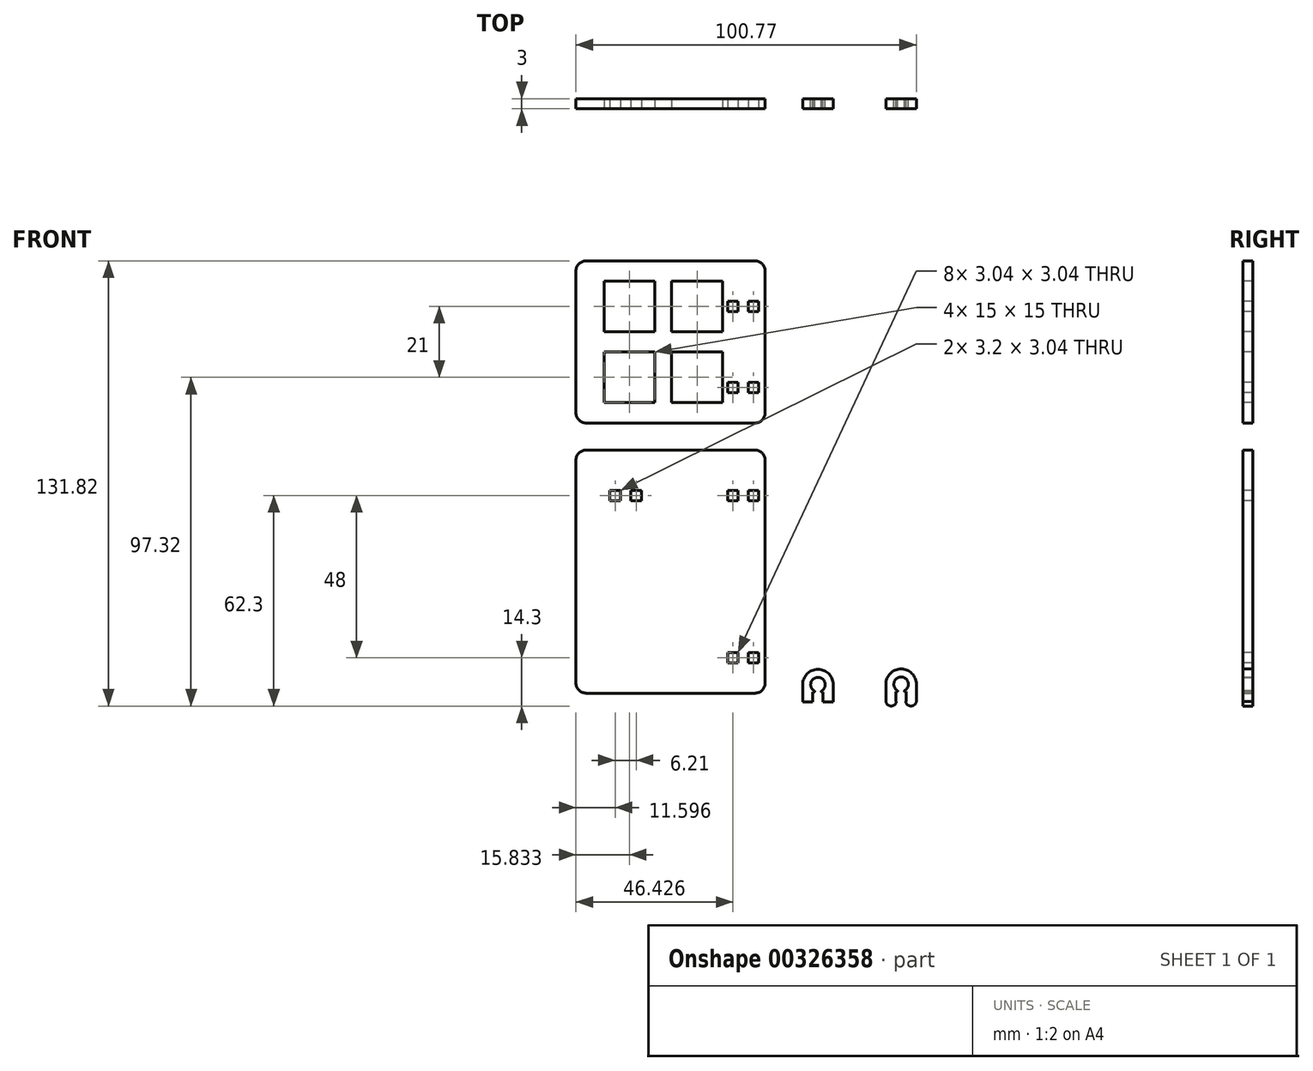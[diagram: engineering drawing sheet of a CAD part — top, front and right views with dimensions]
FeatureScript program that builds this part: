
annotation { "Feature Type Name" : "Feature", "Feature Type Description" : "" }
export const myFeature = defineFeature(function(context is Context, id is Id, definition is map)
    precondition{}
    {
        {
            var Q0;
            Q0=qCreatedBy(makeId("Front.planeOp"),FACE);
            var sketch = newSketch(context, id + "F0", { "sketchPlane" : qUnion([Q0])});
            skArc(sketch, "E0", {"start": v(1.01, 0.63) * mm, "mid": v(0.03, 4.67) * mm, "end": v(-1.07, 0.66) * mm});
            skPoint(sketch, "E0.centerSnap0", {"position": v(-1.52, 2.52) * mm});
            skArc(sketch, "E1", {"start": v(4.53, 2.52) * mm, "mid": v(0, 7.05) * mm, "end": v(-4.53, 2.52) * mm});
            skLineSegment(sketch, "E2", {"start": v(-4.53, 2.52) * mm, "end": v(-4.53, -2.63) * mm});
            skLineSegment(sketch, "E3", {"start": v(4.52, 2.52) * mm, "end": v(4.53, -2.63) * mm});
            skPoint(sketch, "E3.startSnap0", {"position": v(1.52, 2.52) * mm});
            skPoint(sketch, "E4.orphan", {"position": v(-1.52, 4.05) * mm});
            skPoint(sketch, "E5.orphan", {"position": v(1.52, 4.05) * mm});
            skLineSegment(sketch, "E6", {"start": v(-1.08, 0.37) * mm, "end": v(-1.52, 0.37) * mm});
            skLineSegment(sketch, "E7", {"start": v(1.07, 0.37) * mm, "end": v(1.53, 0.37) * mm});
            skArc(sketch, "E8", {"start": v(-1.08, 0.37) * mm, "mid": v(-1, 0.52) * mm, "end": v(-1.08, 0.67) * mm});
            skArc(sketch, "E9", {"start": v(1.01, 0.63) * mm, "mid": v(0.96, 0.47) * mm, "end": v(1.1, 0.37) * mm});
            skPoint(sketch, "E10.orphan", {"position": v(0, 0.37) * mm});
            skPoint(sketch, "E11.start.orphan", {"position": v(-2.15, 2.53) * mm});
            skPoint(sketch, "E12.start.orphan", {"position": v(2.15, 2.53) * mm});
            skLineSegment(sketch, "E13", {"start": v(-1.52, -2.63) * mm, "end": v(-1.52, 0.37) * mm});
            skLineSegment(sketch, "E14", {"start": v(1.53, -2.63) * mm, "end": v(1.53, 0.38) * mm});
            skPoint(sketch, "E15", {"position": v(-1.52, -2.63) * mm});
            skPoint(sketch, "E16", {"position": v(1.53, -2.63) * mm});
            skLineSegment(sketch, "E17", {"start": v(-1.52, -2.63) * mm, "end": v(-4.53, -2.63) * mm});
            skLineSegment(sketch, "E18", {"start": v(1.53, -2.63) * mm, "end": v(4.53, -2.63) * mm});
            skPoint(sketch, "E19.start.orphan", {"position": v(0, 4.05) * mm});
            skArc(sketch, "E20", {"start": v(25.63, 0.75) * mm, "mid": v(24.65, 4.8) * mm, "end": v(23.54, 0.78) * mm});
            skPoint(sketch, "E20.centerSnap0", {"position": v(23.09, 2.64) * mm});
            skArc(sketch, "E21", {"start": v(29.14, 2.64) * mm, "mid": v(24.61, 7.17) * mm, "end": v(20.09, 2.64) * mm});
            skLineSegment(sketch, "E22", {"start": v(20.09, 2.64) * mm, "end": v(20.09, -2.5) * mm});
            skLineSegment(sketch, "E23", {"start": v(29.14, 2.64) * mm, "end": v(29.14, -2.5) * mm});
            skPoint(sketch, "E23.startSnap0", {"position": v(26.14, 2.64) * mm});
            skPoint(sketch, "E24.orphan", {"position": v(23.1, 4.17) * mm});
            skPoint(sketch, "E25.orphan", {"position": v(26.13, 4.16) * mm});
            skLineSegment(sketch, "E26", {"start": v(23.53, 0.5) * mm, "end": v(23.09, 0.5) * mm});
            skLineSegment(sketch, "E27", {"start": v(25.68, 0.5) * mm, "end": v(26.14, 0.5) * mm});
            skArc(sketch, "E28", {"start": v(23.53, 0.5) * mm, "mid": v(23.62, 0.64) * mm, "end": v(23.53, 0.79) * mm});
            skArc(sketch, "E29", {"start": v(25.63, 0.75) * mm, "mid": v(25.57, 0.58) * mm, "end": v(25.72, 0.5) * mm});
            skPoint(sketch, "E30.orphan", {"position": v(24.61, 0.5) * mm});
            skPoint(sketch, "E31.start.orphan", {"position": v(22.46, 2.64) * mm});
            skPoint(sketch, "E32.start.orphan", {"position": v(26.76, 2.64) * mm});
            skLineSegment(sketch, "E33", {"start": v(23.09, -2.5) * mm, "end": v(23.09, 0.5) * mm});
            skLineSegment(sketch, "E34", {"start": v(26.14, -2.5) * mm, "end": v(26.14, 0.5) * mm});
            skPoint(sketch, "E35", {"position": v(23.09, -2.5) * mm});
            skPoint(sketch, "E36", {"position": v(26.14, -2.5) * mm});
            skPoint(sketch, "E37.start.orphan", {"position": v(24.61, 4.17) * mm});
            skLineSegment(sketch, "E38", {"start": v(23.09, -2.5) * mm, "end": v(23.29, -2.5) * mm});
            skLineSegment(sketch, "E39", {"start": v(26.14, -2.5) * mm, "end": v(25.94, -2.5) * mm});
            skArc(sketch, "E40", {"start": v(20.09, -2.5) * mm, "mid": v(21.69, -3.82) * mm, "end": v(23.29, -2.5) * mm});
            skArc(sketch, "E41", {"start": v(25.94, -2.5) * mm, "mid": v(27.54, -3.82) * mm, "end": v(29.14, -2.5) * mm});
            skPoint(sketch, "E42.end.orphan", {"position": v(23.09, -3.5) * mm});
            skPoint(sketch, "E43.orphan", {"position": v(26.14, -3.5) * mm});
            skSolve(sketch);
        }
        {
            var Q0;
            Q0=makeQuery(id+"F0.imprint","IMPRINT",FACE,{"disambiguationData":[TD([[makeQuery(id+"F0.imprint","IMPRINT",EDGE,{"derivedFrom":sQuery(id+"F0.wireOp",EDGE,"E0")}),-1.0]])]});
            var Q1;
            {var subQ1=sQuery(id+"F0.wireOp",EDGE,"E20");Q1=makeQuery(id+"F0.imprint","IMPRINT",FACE,{"disambiguationData":[TD([[makeQuery(id+"F0.imprint","IMPRINT",EDGE,{"derivedFrom":subQ1}),-1.0]])]});}
            extrude(context, id + "F1", {"entities" : qUnion([Q0, Q1]), "depth" : 3 * mm});
        }
        {
            var Q0;
            Q0=qCreatedBy(makeId("Front.planeOp"),FACE);
            var sketch = newSketch(context, id + "F2", { "sketchPlane" : qUnion([Q0])});
            skLineSegment(sketch, "E44.bottom", {"start": v(-71.63, 0) * mm, "end": v(-15.63, 0) * mm});
            skLineSegment(sketch, "E44.left", {"start": v(-71.63, 0) * mm, "end": v(-71.63, 72) * mm});
            skLineSegment(sketch, "E44.right", {"start": v(-15.63, 0) * mm, "end": v(-15.63, 72) * mm});
            skLineSegment(sketch, "E45", {"start": v(-71.63, 80) * mm, "end": v(-71.63, 128) * mm});
            skLineSegment(sketch, "E46", {"start": v(-15.63, 80) * mm, "end": v(-15.63, 128) * mm});
            skLineSegment(sketch, "E47", {"start": v(-15.63, 128) * mm, "end": v(-71.63, 128) * mm});
            skLineSegment(sketch, "E48", {"start": v(-71.63, 72) * mm, "end": v(-15.63, 72) * mm});
            skLineSegment(sketch, "E49", {"start": v(-71.63, 80) * mm, "end": v(-15.63, 80) * mm});
            skSolve(sketch);
        }
        {
            var Q0;
            Q0=makeQuery(id+"F2.imprint","IMPRINT",FACE,{"disambiguationData":[TD([[makeQuery(id+"F2.imprint","IMPRINT",EDGE,{"derivedFrom":sQuery(id+"F2.wireOp",EDGE,"E45")}),-1.0]])]});
            var Q1;
            Q1=makeQuery(id+"F2.imprint","IMPRINT",FACE,{"disambiguationData":[TD([[makeQuery(id+"F2.imprint","IMPRINT",EDGE,{"derivedFrom":sQuery(id+"F2.wireOp",EDGE,"E44.bottom")}),1.0]])]});
            extrude(context, id + "F3", {"entities" : qUnion([Q0, Q1]), "depth" : 3 * mm});
        }
        {
            var Q0;
            Q0=makeQuery(id+"F3.opExtrude","CAP_FACE",FACE,{"disambiguationData":[OSD([sQuery(id+"F2.wireOp",EDGE,"E45"),sQuery(id+"F2.wireOp",EDGE,"E46"),sQuery(id+"F2.wireOp",EDGE,"E47"),sQuery(id+"F2.wireOp",EDGE,"E49")])],"isStart":false});
            var sketch = newSketch(context, id + "F4", { "sketchPlane" : qUnion([Q0])});
            skLineSegment(sketch, "E50.bottom", {"start": v(-23.68, 12) * mm, "end": v(-26.72, 12) * mm});
            skLineSegment(sketch, "E50.top", {"start": v(-23.68, 8.96) * mm, "end": v(-26.72, 8.96) * mm});
            skLineSegment(sketch, "E50.left", {"start": v(-23.68, 12) * mm, "end": v(-23.68, 8.96) * mm});
            skLineSegment(sketch, "E50.right", {"start": v(-26.72, 12) * mm, "end": v(-26.72, 8.96) * mm});
            skLineSegment(sketch, "E51.bottom", {"start": v(-20.67, 12) * mm, "end": v(-17.63, 12) * mm});
            skLineSegment(sketch, "E51.top", {"start": v(-20.67, 8.96) * mm, "end": v(-17.63, 8.96) * mm});
            skLineSegment(sketch, "E51.left", {"start": v(-20.67, 12) * mm, "end": v(-20.67, 8.96) * mm});
            skLineSegment(sketch, "E51.right", {"start": v(-17.63, 12) * mm, "end": v(-17.63, 8.96) * mm});
            skLineSegment(sketch, "E52.bottom", {"start": v(-23.68, 60) * mm, "end": v(-26.72, 60) * mm});
            skLineSegment(sketch, "E52.top", {"start": v(-23.68, 56.96) * mm, "end": v(-26.72, 56.96) * mm});
            skLineSegment(sketch, "E52.left", {"start": v(-23.68, 60) * mm, "end": v(-23.68, 56.96) * mm});
            skLineSegment(sketch, "E52.right", {"start": v(-26.72, 60) * mm, "end": v(-26.72, 56.96) * mm});
            skLineSegment(sketch, "E53.bottom", {"start": v(-20.67, 60) * mm, "end": v(-17.63, 60) * mm});
            skLineSegment(sketch, "E53.top", {"start": v(-20.67, 56.96) * mm, "end": v(-17.63, 56.96) * mm});
            skLineSegment(sketch, "E53.left", {"start": v(-20.67, 60) * mm, "end": v(-20.67, 56.96) * mm});
            skLineSegment(sketch, "E53.right", {"start": v(-17.63, 60) * mm, "end": v(-17.63, 56.96) * mm});
            skLineSegment(sketch, "E54.bottom", {"start": v(-23.68, 92) * mm, "end": v(-26.72, 92) * mm});
            skLineSegment(sketch, "E54.top", {"start": v(-23.68, 88.96) * mm, "end": v(-26.72, 88.96) * mm});
            skLineSegment(sketch, "E54.left", {"start": v(-23.68, 92) * mm, "end": v(-23.68, 88.96) * mm});
            skLineSegment(sketch, "E54.right", {"start": v(-26.72, 92) * mm, "end": v(-26.72, 88.96) * mm});
            skLineSegment(sketch, "E55.bottom", {"start": v(-20.67, 92) * mm, "end": v(-17.63, 92) * mm});
            skLineSegment(sketch, "E55.top", {"start": v(-20.67, 88.96) * mm, "end": v(-17.63, 88.96) * mm});
            skLineSegment(sketch, "E55.left", {"start": v(-20.67, 92) * mm, "end": v(-20.67, 88.96) * mm});
            skLineSegment(sketch, "E55.right", {"start": v(-17.63, 92) * mm, "end": v(-17.63, 88.96) * mm});
            skLineSegment(sketch, "E56.bottom", {"start": v(-23.68, 116) * mm, "end": v(-26.72, 116) * mm});
            skLineSegment(sketch, "E56.top", {"start": v(-23.68, 112.96) * mm, "end": v(-26.72, 112.96) * mm});
            skLineSegment(sketch, "E56.left", {"start": v(-23.68, 116) * mm, "end": v(-23.68, 112.96) * mm});
            skLineSegment(sketch, "E56.right", {"start": v(-26.72, 116) * mm, "end": v(-26.72, 112.96) * mm});
            skLineSegment(sketch, "E57.bottom", {"start": v(-20.67, 116) * mm, "end": v(-17.63, 116) * mm});
            skLineSegment(sketch, "E57.top", {"start": v(-20.67, 112.96) * mm, "end": v(-17.63, 112.96) * mm});
            skLineSegment(sketch, "E57.left", {"start": v(-20.67, 116) * mm, "end": v(-20.67, 112.96) * mm});
            skLineSegment(sketch, "E57.right", {"start": v(-17.63, 116) * mm, "end": v(-17.63, 112.96) * mm});
            skLineSegment(sketch, "E58.bottom", {"start": v(-58.43, 60) * mm, "end": v(-61.63, 60) * mm});
            skLineSegment(sketch, "E58.top", {"start": v(-58.43, 56.96) * mm, "end": v(-61.63, 56.96) * mm});
            skLineSegment(sketch, "E58.left", {"start": v(-58.43, 60) * mm, "end": v(-58.43, 56.96) * mm});
            skLineSegment(sketch, "E58.right", {"start": v(-61.63, 60) * mm, "end": v(-61.63, 56.96) * mm});
            skLineSegment(sketch, "E59.bottom", {"start": v(-55.42, 60) * mm, "end": v(-52.22, 60) * mm});
            skLineSegment(sketch, "E59.top", {"start": v(-55.42, 56.96) * mm, "end": v(-52.22, 56.96) * mm});
            skLineSegment(sketch, "E59.left", {"start": v(-55.42, 60) * mm, "end": v(-55.42, 56.96) * mm});
            skLineSegment(sketch, "E59.right", {"start": v(-52.22, 60) * mm, "end": v(-52.22, 56.96) * mm});
            skSolve(sketch);
        }
        {
            var Q0;
            Q0=makeQuery(id+"F4.imprint","IMPRINT",FACE,{"disambiguationData":[TD([[makeQuery(id+"F4.imprint","IMPRINT",EDGE,{"derivedFrom":sQuery(id+"F4.wireOp",EDGE,"E56.bottom")}),1.0]])]});
            var Q1;
            Q1=makeQuery(id+"F4.imprint","IMPRINT",FACE,{"disambiguationData":[TD([[makeQuery(id+"F4.imprint","IMPRINT",EDGE,{"derivedFrom":sQuery(id+"F4.wireOp",EDGE,"E57.bottom")}),-1.0]])]});
            var Q2;
            Q2=makeQuery(id+"F4.imprint","IMPRINT",FACE,{"disambiguationData":[TD([[makeQuery(id+"F4.imprint","IMPRINT",EDGE,{"derivedFrom":sQuery(id+"F4.wireOp",EDGE,"E54.bottom")}),1.0]])]});
            var Q3;
            Q3=makeQuery(id+"F4.imprint","IMPRINT",FACE,{"disambiguationData":[TD([[makeQuery(id+"F4.imprint","IMPRINT",EDGE,{"derivedFrom":sQuery(id+"F4.wireOp",EDGE,"E55.bottom")}),-1.0]])]});
            var Q4;
            Q4=makeQuery(id+"F4.imprint","IMPRINT",FACE,{"disambiguationData":[TD([[makeQuery(id+"F4.imprint","IMPRINT",EDGE,{"derivedFrom":sQuery(id+"F4.wireOp",EDGE,"E52.bottom")}),1.0]])]});
            var Q5;
            Q5=makeQuery(id+"F4.imprint","IMPRINT",FACE,{"disambiguationData":[TD([[makeQuery(id+"F4.imprint","IMPRINT",EDGE,{"derivedFrom":sQuery(id+"F4.wireOp",EDGE,"E53.bottom")}),-1.0]])]});
            var Q6;
            Q6=makeQuery(id+"F4.imprint","IMPRINT",FACE,{"disambiguationData":[TD([[makeQuery(id+"F4.imprint","IMPRINT",EDGE,{"derivedFrom":sQuery(id+"F4.wireOp",EDGE,"E50.bottom")}),1.0]])]});
            var Q7;
            Q7=makeQuery(id+"F4.imprint","IMPRINT",FACE,{"disambiguationData":[TD([[makeQuery(id+"F4.imprint","IMPRINT",EDGE,{"derivedFrom":sQuery(id+"F4.wireOp",EDGE,"E51.bottom")}),-1.0]])]});
            extrude(context, id + "F5", {"entities" : qUnion([Q0, Q1, Q2, Q3, Q4, Q5, Q6, Q7]), "operationType" : NewBodyOperationType.REMOVE, "endBound" : BoundingType.THROUGH_ALL, "oppositeDirection" : true, "depth" : 25 * mm});
        }
        {
            var Q0;
            Q0 = qSketchRegion(id + "F4", true);
            extrude(context, id + "F6", {"entities" : qUnion([Q0]), "operationType" : NewBodyOperationType.REMOVE, "oppositeDirection" : true, "depth" : 25 * mm});
        }
        {
            var Q0;
            Q0=makeQuery(id+"F3.opExtrude","CAP_FACE",FACE,{"disambiguationData":[OSD([sQuery(id+"F2.wireOp",EDGE,"E45"),sQuery(id+"F2.wireOp",EDGE,"E46"),sQuery(id+"F2.wireOp",EDGE,"E47"),sQuery(id+"F2.wireOp",EDGE,"E49")])],"isStart":false});
            var sketch = newSketch(context, id + "F7", { "sketchPlane" : qUnion([Q0])});
            skLineSegment(sketch, "E60.bottom", {"start": v(-63.3, 122) * mm, "end": v(-48.3, 122) * mm});
            skLineSegment(sketch, "E60.top", {"start": v(-63.3, 107) * mm, "end": v(-48.3, 107) * mm});
            skLineSegment(sketch, "E60.left", {"start": v(-63.3, 122) * mm, "end": v(-63.3, 107) * mm});
            skLineSegment(sketch, "E60.right", {"start": v(-48.3, 122) * mm, "end": v(-48.3, 107) * mm});
            skLineSegment(sketch, "E61.bottom", {"start": v(-43.3, 122) * mm, "end": v(-28.3, 122) * mm});
            skLineSegment(sketch, "E61.top", {"start": v(-43.3, 107) * mm, "end": v(-28.3, 107) * mm});
            skLineSegment(sketch, "E61.left", {"start": v(-43.3, 122) * mm, "end": v(-43.3, 107) * mm});
            skLineSegment(sketch, "E61.right", {"start": v(-28.3, 122) * mm, "end": v(-28.3, 107) * mm});
            skLineSegment(sketch, "E62.bottom", {"start": v(-63.3, 101) * mm, "end": v(-48.3, 101) * mm});
            skLineSegment(sketch, "E62.top", {"start": v(-63.3, 86) * mm, "end": v(-48.3, 86) * mm});
            skLineSegment(sketch, "E62.left", {"start": v(-63.3, 101) * mm, "end": v(-63.3, 86) * mm});
            skLineSegment(sketch, "E62.right", {"start": v(-48.3, 101) * mm, "end": v(-48.3, 86) * mm});
            skLineSegment(sketch, "E63.bottom", {"start": v(-43.3, 101) * mm, "end": v(-28.3, 101) * mm});
            skLineSegment(sketch, "E63.top", {"start": v(-43.3, 86) * mm, "end": v(-28.3, 86) * mm});
            skLineSegment(sketch, "E63.left", {"start": v(-43.3, 101) * mm, "end": v(-43.3, 86) * mm});
            skLineSegment(sketch, "E63.right", {"start": v(-28.3, 101) * mm, "end": v(-28.3, 86) * mm});
            skSolve(sketch);
        }
        {
            var Q0;
            Q0=makeQuery(id+"F7.imprint","IMPRINT",FACE,{"disambiguationData":[TD([[makeQuery(id+"F7.imprint","IMPRINT",EDGE,{"derivedFrom":sQuery(id+"F7.wireOp",EDGE,"E60.bottom")}),-1.0]])]});
            var Q1;
            Q1=makeQuery(id+"F7.imprint","IMPRINT",FACE,{"disambiguationData":[TD([[makeQuery(id+"F7.imprint","IMPRINT",EDGE,{"derivedFrom":sQuery(id+"F7.wireOp",EDGE,"E61.bottom")}),-1.0]])]});
            var Q2;
            Q2=makeQuery(id+"F7.imprint","IMPRINT",FACE,{"disambiguationData":[TD([[makeQuery(id+"F7.imprint","IMPRINT",EDGE,{"derivedFrom":sQuery(id+"F7.wireOp",EDGE,"E63.bottom")}),-1.0]])]});
            var Q3;
            Q3=makeQuery(id+"F7.imprint","IMPRINT",FACE,{"disambiguationData":[TD([[makeQuery(id+"F7.imprint","IMPRINT",EDGE,{"derivedFrom":sQuery(id+"F7.wireOp",EDGE,"E62.bottom")}),-1.0]])]});
            extrude(context, id + "F8", {"entities" : qUnion([Q0, Q1, Q2, Q3]), "operationType" : NewBodyOperationType.REMOVE, "endBound" : BoundingType.THROUGH_ALL, "oppositeDirection" : true, "depth" : 25 * mm});
        }
        {
            var Q0;
            Q0=makeQuery(id+"F3.opExtrude","SWEPT_EDGE",EDGE,{"disambiguationData":[OSD([sQuery(id+"F2.wireOp",EDGE,"E45"),sQuery(id+"F2.wireOp",EDGE,"E47")])]});
            var Q1;
            Q1=makeQuery(id+"F3.opExtrude","SWEPT_EDGE",EDGE,{"disambiguationData":[OSD([sQuery(id+"F2.wireOp",EDGE,"E44.left"),sQuery(id+"F2.wireOp",EDGE,"E48")])]});
            var Q2;
            Q2=makeQuery(id+"F3.opExtrude","SWEPT_EDGE",EDGE,{"disambiguationData":[OSD([sQuery(id+"F2.wireOp",EDGE,"E44.right"),sQuery(id+"F2.wireOp",EDGE,"E48")])]});
            var Q3;
            Q3=makeQuery(id+"F3.opExtrude","SWEPT_EDGE",EDGE,{"disambiguationData":[OSD([sQuery(id+"F2.wireOp",EDGE,"E45"),sQuery(id+"F2.wireOp",EDGE,"E49")])]});
            var Q4;
            Q4=makeQuery(id+"F3.opExtrude","SWEPT_EDGE",EDGE,{"disambiguationData":[OSD([sQuery(id+"F2.wireOp",EDGE,"E46"),sQuery(id+"F2.wireOp",EDGE,"E49")])]});
            var Q5;
            Q5=makeQuery(id+"F3.opExtrude","SWEPT_EDGE",EDGE,{"disambiguationData":[OSD([sQuery(id+"F2.wireOp",EDGE,"E46"),sQuery(id+"F2.wireOp",EDGE,"E47")])]});
            var Q6;
            Q6=makeQuery(id+"F3.opExtrude","SWEPT_EDGE",EDGE,{"disambiguationData":[OSD([sQuery(id+"F2.wireOp",EDGE,"E44.bottom"),sQuery(id+"F2.wireOp",EDGE,"E44.left")])]});
            var Q7;
            Q7=makeQuery(id+"F3.opExtrude","SWEPT_EDGE",EDGE,{"disambiguationData":[OSD([sQuery(id+"F2.wireOp",EDGE,"E44.bottom"),sQuery(id+"F2.wireOp",EDGE,"E44.right")])]});
            fillet(context, id + "F9", {"entities" : qUnion([Q0, Q1, Q2, Q3, Q4, Q5, Q6, Q7]), "radius" : 3 * mm, "tangentPropagation" : true, "allowEdgeOverflow" : false});
        }
    });
